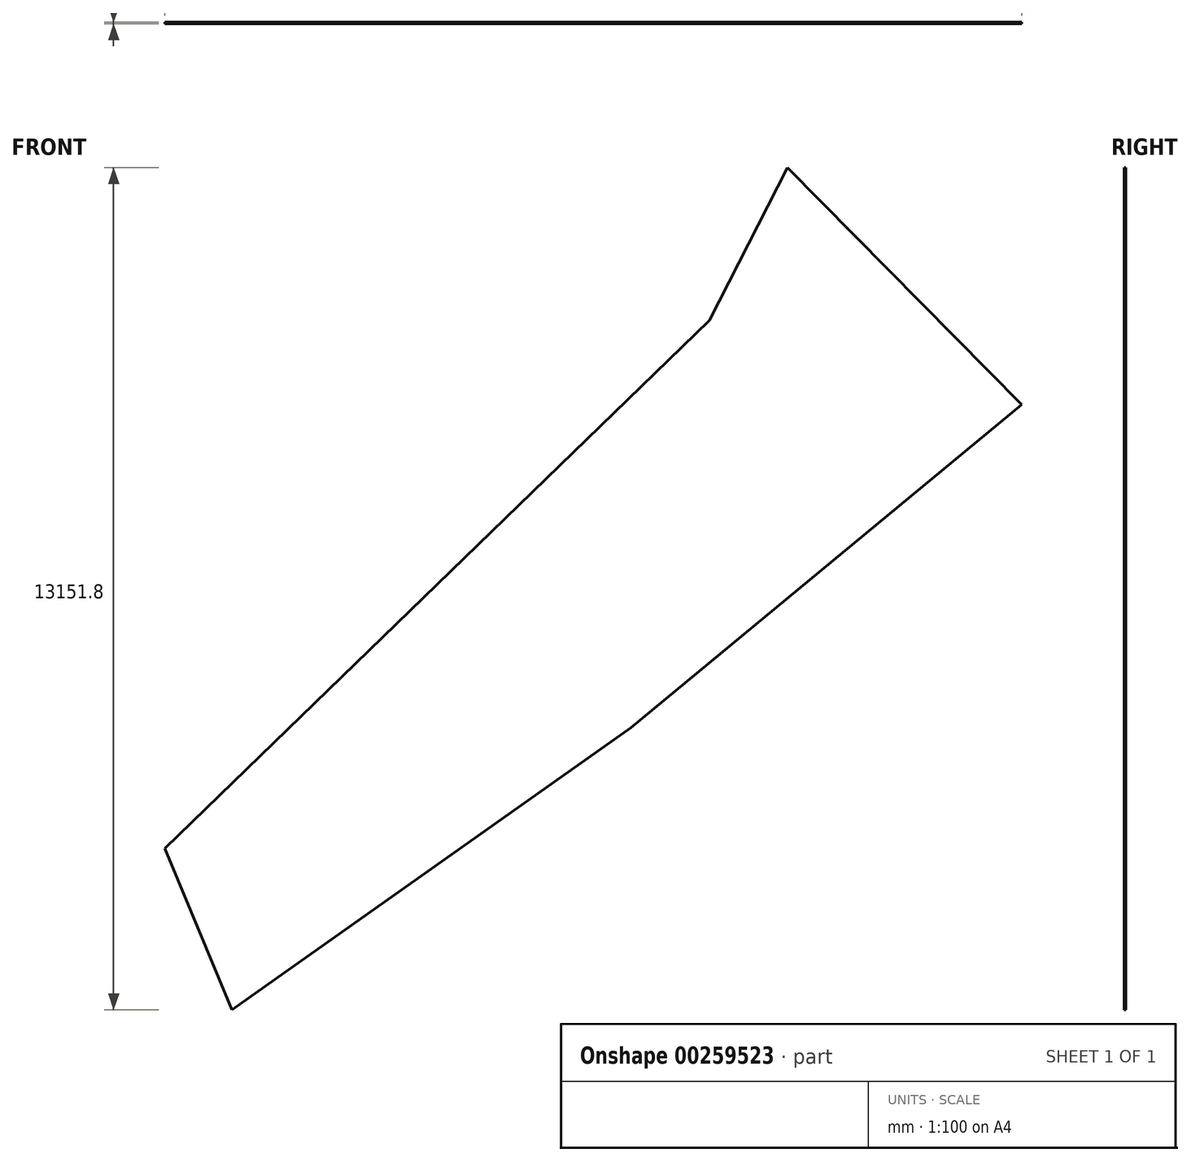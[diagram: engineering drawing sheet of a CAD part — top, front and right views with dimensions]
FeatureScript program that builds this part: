
annotation { "Feature Type Name" : "Feature", "Feature Type Description" : "" }
export const myFeature = defineFeature(function(context is Context, id is Id, definition is map)
    precondition{}
    {
        {
            var Q0;
            Q0=qCreatedBy(makeId("Front.planeOp"),FACE);
            var sketch = newSketch(context, id + "F0", { "sketchPlane" : qUnion([Q0])});
            skLineSegment(sketch, "E0.0", {"start": v(-5712.25, -11460) * mm, "end": v(2787.37, -3213.7) * mm});
            skLineSegment(sketch, "E0.1", {"start": v(4007.12, -828.97) * mm, "end": v(7665.16, -4525.52) * mm});
            skLineSegment(sketch, "E0.2", {"start": v(7665.16, -4525.52) * mm, "end": v(1563.68, -9575.03) * mm});
            skLineSegment(sketch, "E0.3", {"start": v(2787.37, -3213.7) * mm, "end": v(4007.12, -828.97) * mm});
            skLineSegment(sketch, "E0.4", {"start": v(1563.68, -9575.03) * mm, "end": v(-4665.17, -13980.8) * mm});
            skLineSegment(sketch, "E0.5", {"start": v(-4665.17, -13980.8) * mm, "end": v(-5712.25, -11460) * mm});
            skSolve(sketch);
        }
        {
            var Q0;
            Q0 = qSketchRegion(id + "F0", true);
            extrude(context, id + "F1", {"entities" : qUnion([Q0]), "depth" : 25 * mm});
        }
    });
